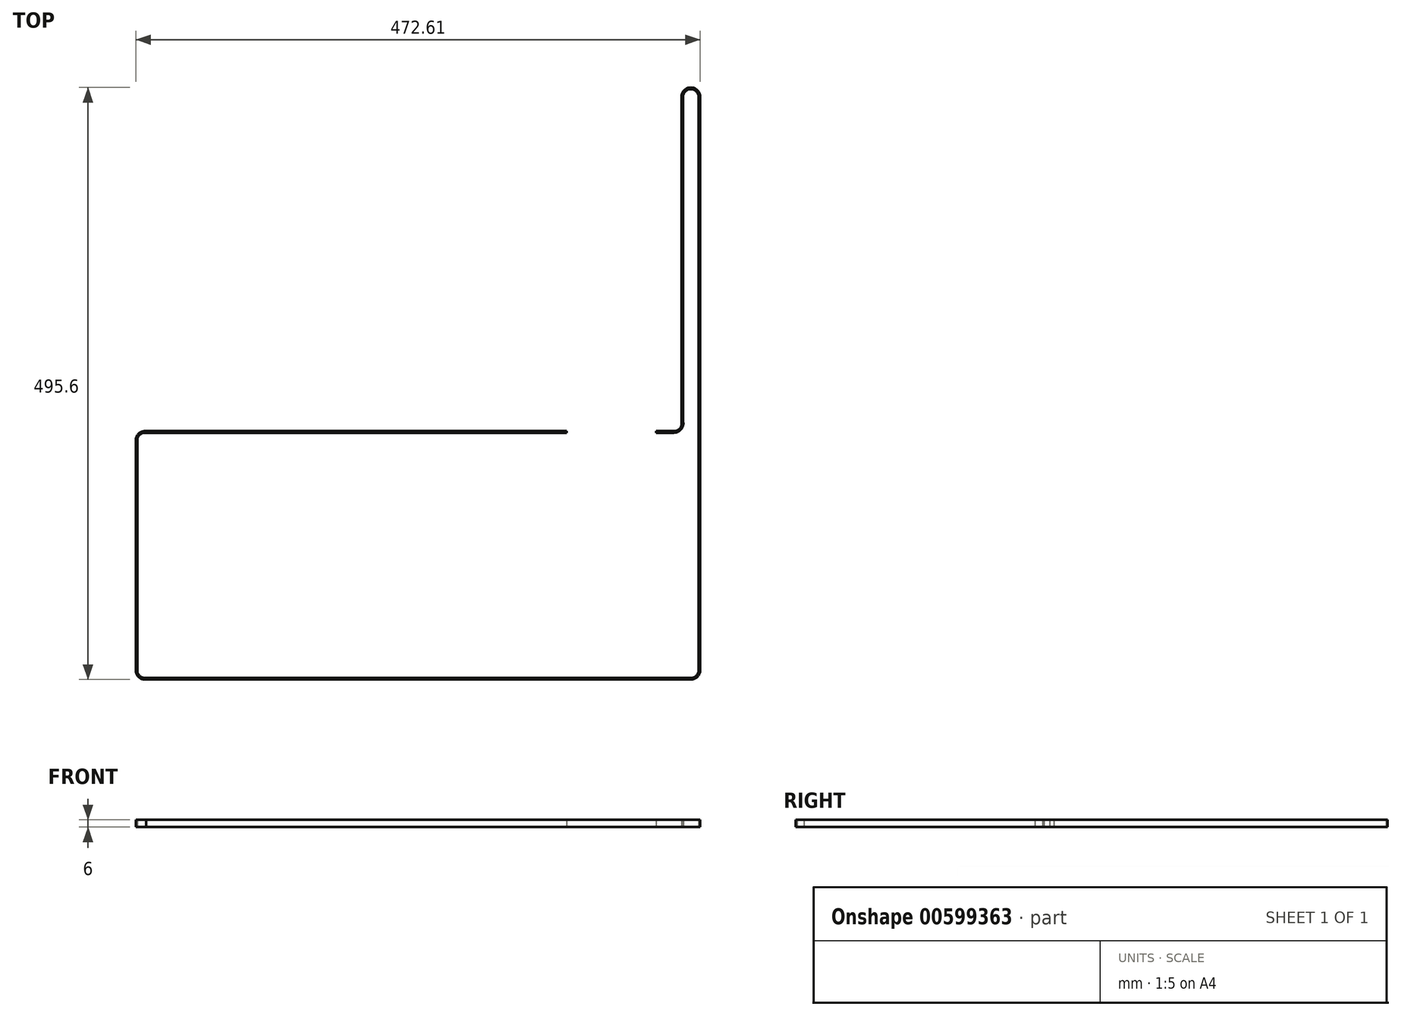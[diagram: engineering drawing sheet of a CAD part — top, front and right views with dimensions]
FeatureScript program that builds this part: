
annotation { "Feature Type Name" : "Feature", "Feature Type Description" : "" }
export const myFeature = defineFeature(function(context is Context, id is Id, definition is map)
    precondition{}
    {
        {
            var Q0;
            Q0=qCreatedBy(makeId("Top.planeOp"),FACE);
            var sketch = newSketch(context, id + "F0", { "sketchPlane" : qUnion([Q0])});
            skArc(sketch, "E0.4", {"start": v(-466.98, -110.48) * mm, "mid": v(-465.07, -115.07) * mm, "end": v(-460.48, -116.98) * mm});
            skArc(sketch, "E0.5", {"start": v(-3.46, -116.98) * mm, "mid": v(1.14, -115.07) * mm, "end": v(3.04, -110.48) * mm});
            skArc(sketch, "E1", {"start": v(-460.48, 88.37) * mm, "mid": v(-465.07, 86.47) * mm, "end": v(-466.98, 81.87) * mm});
            skArc(sketch, "E2", {"start": v(-17.56, 88.37) * mm, "mid": v(-11.45, 91.32) * mm, "end": v(-9.96, 97.95) * mm});
            skLineSegment(sketch, "E3", {"start": v(-17.56, 88.37) * mm, "end": v(-32.56, 88.37) * mm});
            skLineSegment(sketch, "E4", {"start": v(-460.48, -116.98) * mm, "end": v(-3.46, -116.98) * mm});
            skLineSegment(sketch, "E5", {"start": v(-466.98, -110.48) * mm, "end": v(-466.98, 81.87) * mm});
            skLineSegment(sketch, "E6", {"start": v(-460.48, 88.37) * mm, "end": v(-243.54, 88.37) * mm});
            skArc(sketch, "E7.0", {"start": v(-17.56, 89.67) * mm, "mid": v(-13.57, 91.04) * mm, "end": v(-11.26, 94.55) * mm});
            skArc(sketch, "E8.0", {"start": v(-460.2, 89.67) * mm, "mid": v(-465.79, 87.59) * mm, "end": v(-468.27, 82.16) * mm});
            skArc(sketch, "E9.0", {"start": v(-468.23, -111.36) * mm, "mid": v(-465.33, -116.58) * mm, "end": v(-459.6, -118.23) * mm});
            skArc(sketch, "E10.0", {"start": v(-3.46, -118.28) * mm, "mid": v(2.05, -116) * mm, "end": v(4.34, -110.48) * mm});
            skLineSegment(sketch, "E11", {"start": v(-3.46, -118.28) * mm, "end": v(-459.6, -118.23) * mm});
            skLineSegment(sketch, "E12", {"start": v(-468.23, -111.36) * mm, "end": v(-468.27, 82.16) * mm});
            skLineSegment(sketch, "E13", {"start": v(-460.2, 89.67) * mm, "end": v(-442.94, 89.67) * mm});
            skLineSegment(sketch, "E14", {"start": v(-17.56, 89.67) * mm, "end": v(-32.56, 89.67) * mm});
            skLineSegment(sketch, "E15", {"start": v(-11.26, 94.55) * mm, "end": v(-11.26, 369.52) * mm});
            skLineSegment(sketch, "E16.trimOffspring", {"start": v(-9.96, 369.52) * mm, "end": v(-9.96, 97.95) * mm});
            skArc(sketch, "E17", {"start": v(4.34, 369.52) * mm, "mid": v(-3.46, 377.32) * mm, "end": v(-11.26, 369.52) * mm});
            skArc(sketch, "E18", {"start": v(3.04, 369.52) * mm, "mid": v(-3.46, 376.02) * mm, "end": v(-9.96, 369.52) * mm});
            skLineSegment(sketch, "E19", {"start": v(4.34, -110.48) * mm, "end": v(4.34, 369.52) * mm});
            skLineSegment(sketch, "E20", {"start": v(3.04, -110.48) * mm, "end": v(3.04, 369.52) * mm});
            skLineSegment(sketch, "E21", {"start": v(-32.56, 89.67) * mm, "end": v(-32.56, 88.37) * mm});
            skLineSegment(sketch, "E22", {"start": v(-107.56, 89.67) * mm, "end": v(-107.56, 88.37) * mm});
            skLineSegment(sketch, "E23.trimOffspring", {"start": v(-107.56, 89.67) * mm, "end": v(-442.94, 89.67) * mm});
            skLineSegment(sketch, "E24.trimOffspring", {"start": v(-107.56, 88.37) * mm, "end": v(-243.54, 88.37) * mm});
            skSolve(sketch);
        }
        {
            var Q0;
            Q0=qSketchRegion(id+"F0",true);
            extrude(context, id + "F1", {"entities" : qUnion([Q0]), "depth" : 6 * mm});
        }
    });
